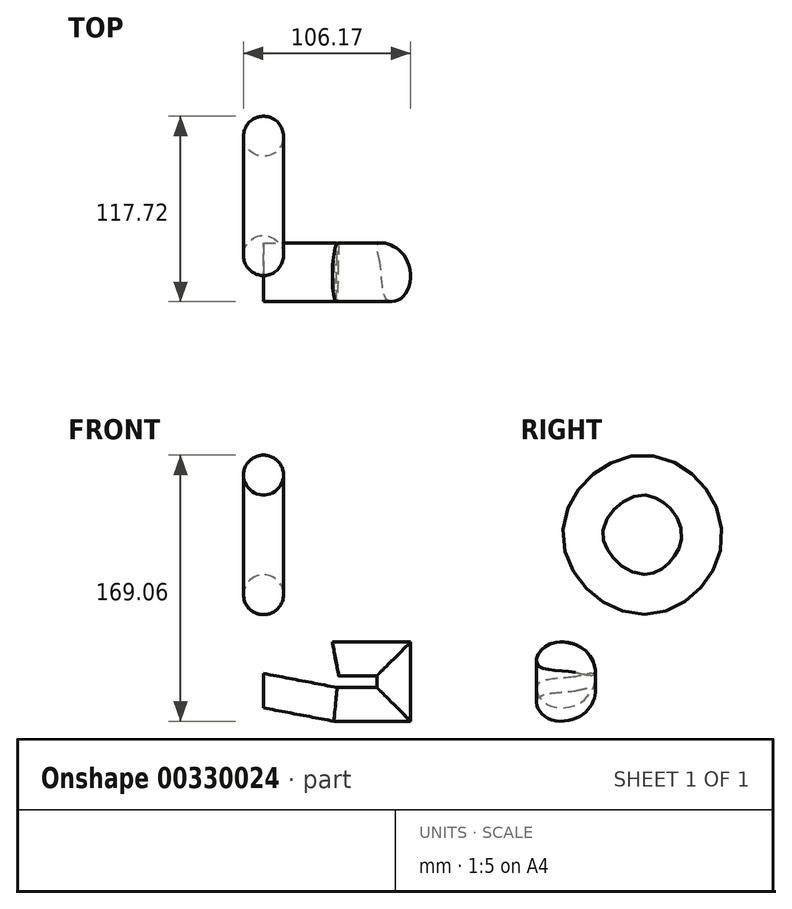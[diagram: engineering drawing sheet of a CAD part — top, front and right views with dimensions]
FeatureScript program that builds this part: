
annotation { "Feature Type Name" : "Feature", "Feature Type Description" : "" }
export const myFeature = defineFeature(function(context is Context, id is Id, definition is map)
    precondition{}
    {
        {
            var Q0;
            Q0=qCreatedBy(makeId("Front.planeOp"),FACE);
            var sketch = newSketch(context, id + "F0", { "sketchPlane" : qUnion([Q0])});
            skCircle(sketch, "E0", {"center": v(0, 0) * mm, "radius": 12.7 * mm});
            skSolve(sketch);
        }
        {
            var Q0;
            Q0=qCreatedBy(makeId("Right.planeOp"),FACE);
            var sketch = newSketch(context, id + "F1", { "sketchPlane" : qUnion([Q0])});
            skFitSpline(sketch, "E1", {"points": [v(0, 0) * mm, v(-39.12, 38.94) * mm, v(0, 75.93) * mm, v(36.63, 37.88) * mm, v(0, 0) * mm]});
            skSolve(sketch);
        }
        {
            var Q0;
            Q0=makeQuery(id+"F0.imprint","IMPRINT",FACE,{"disambiguationData":[TD([[makeQuery(id+"F0.imprint","IMPRINT",EDGE,{"derivedFrom":sQuery(id+"F0.wireOp",EDGE,"E0")}),1.0]])]});
            var Q1;
            Q1=sQuery(id+"F1.wireOp",EDGE,"E1");
            sweep(context, id + "F2", {"profiles" : qUnion([Q0]), "path" : qUnion([Q1])});
        }
        {
            var Q0;
            Q0=qCreatedBy(makeId("Right.planeOp"),FACE);
            var sketch = newSketch(context, id + "F3", { "sketchPlane" : qUnion([Q0])});
            skFitSpline(sketch, "E2", {"points": [v(-43.8, -52.16) * mm, v(-67.6, -57.17) * mm, v(-61.76, -69.7) * mm, v(-37.12, -65.94) * mm, v(-31.7, -50.9) * mm, v(-43.8, -52.16) * mm]});
            skSolve(sketch);
        }
        {
            var Q0;
            Q0=qCreatedBy(makeId("Front.planeOp"),FACE);
            var sketch = newSketch(context, id + "F4", { "sketchPlane" : qUnion([Q0])});
            skFitSpline(sketch, "E3", {"points": [v(0, -61.45) * mm, v(45.69, -70.14) * mm], "startDerivative": vector(45.69, -8.7) * mm, "endDerivative": vector(45.69, -8.7) * mm});
            skLineSegment(sketch, "E4.bottom", {"start": v(45.69, -70.14) * mm, "end": v(83.19, -70.14) * mm});
            skLineSegment(sketch, "E4.top", {"start": v(45.69, -40.34) * mm, "end": v(83.19, -40.34) * mm});
            skLineSegment(sketch, "E4.left", {"start": v(45.69, -70.14) * mm, "end": v(45.69, -40.34) * mm});
            skLineSegment(sketch, "E4.right", {"start": v(83.19, -70.14) * mm, "end": v(83.19, -40.34) * mm});
            skSolve(sketch);
        }
        {
            var Q0;
            Q0=makeQuery(id+"F3.imprint","IMPRINT",FACE,{"disambiguationData":[TD([[makeQuery(id+"F3.imprint","IMPRINT",EDGE,{"derivedFrom":sQuery(id+"F3.wireOp",EDGE,"E2")}),1.0]])]});
            var Q1;
            Q1=sQuery(id+"F4.wireOp",EDGE,"E3");
            var Q2;
            Q2=sQuery(id+"F4.wireOp",EDGE,"E4.bottom");
            var Q3;
            Q3=sQuery(id+"F4.wireOp",EDGE,"E4.right");
            var Q4;
            Q4=sQuery(id+"F4.wireOp",EDGE,"E4.top");
            sweep(context, id + "F5", {"profiles" : qUnion([Q0]), "path" : qUnion([Q1, Q2, Q3, Q4])});
        }
    });
